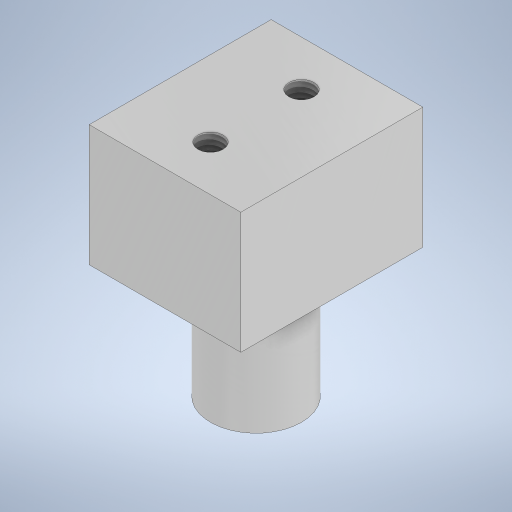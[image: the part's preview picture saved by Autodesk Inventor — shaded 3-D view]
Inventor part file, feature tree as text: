
AUTODESK INVENTOR PART (.ipt)
format: ipt  version: 2023 (Build 270158000, 158)  size: 270,336 bytes
history: native  units: mm
features: sketch x4, extrude x2, hole x2, other x1
ambient origin geometry x8: Origin, YZ Plane, XZ Plane, XY Plane, X Axis, Y Axis, Z Axis, Center Point
bodies: Body1 (feature_tree)
feature tree (9):
  other  "Sólido1"
  extrude  "Extrusão1"  Depth=30.0mm
  hole  "Furo1"  [1 undecoded]
  extrude  "Extrusão2"  Depth=12.5mm
  hole  "Furo3"  [1 undecoded]
  sketch  "Esboço1"  dims[d0=25.0mm d1=30.0mm]
  sketch  "Esboço2"  dims[d2=20.0mm d3=0.0mm d4=25.0mm]
  sketch  "Esboço3"  dims[d5=12.5mm d6=12.5mm]
  sketch  "Esboço5"  dims[d9=4.134mm d10=10.0mm d11=4.0mm d12=2.0mm d13=90.0deg d14=14.2mm d15=20.594885mm d16=25.0mm d17=30.0mm d18=12.5mm d19=15.0mm d21=15.0mm d22=20.0mm d23=0.0mm d31=7.5mm d32=7.5mm d33=8.376mm d34=17.0mm d35=0.624793mm d36=10.589mm d37=4.0mm d38=2.0mm d39=90.0deg d40=20.0mm d41=20.594885mm d24=0.5mm d25=0.872665mm]
note: 2 required parameter values undecoded (feature->parameter linkage not recoverable at this tier; creation-order binding heuristic only, values carry confidence <= 0.55)
